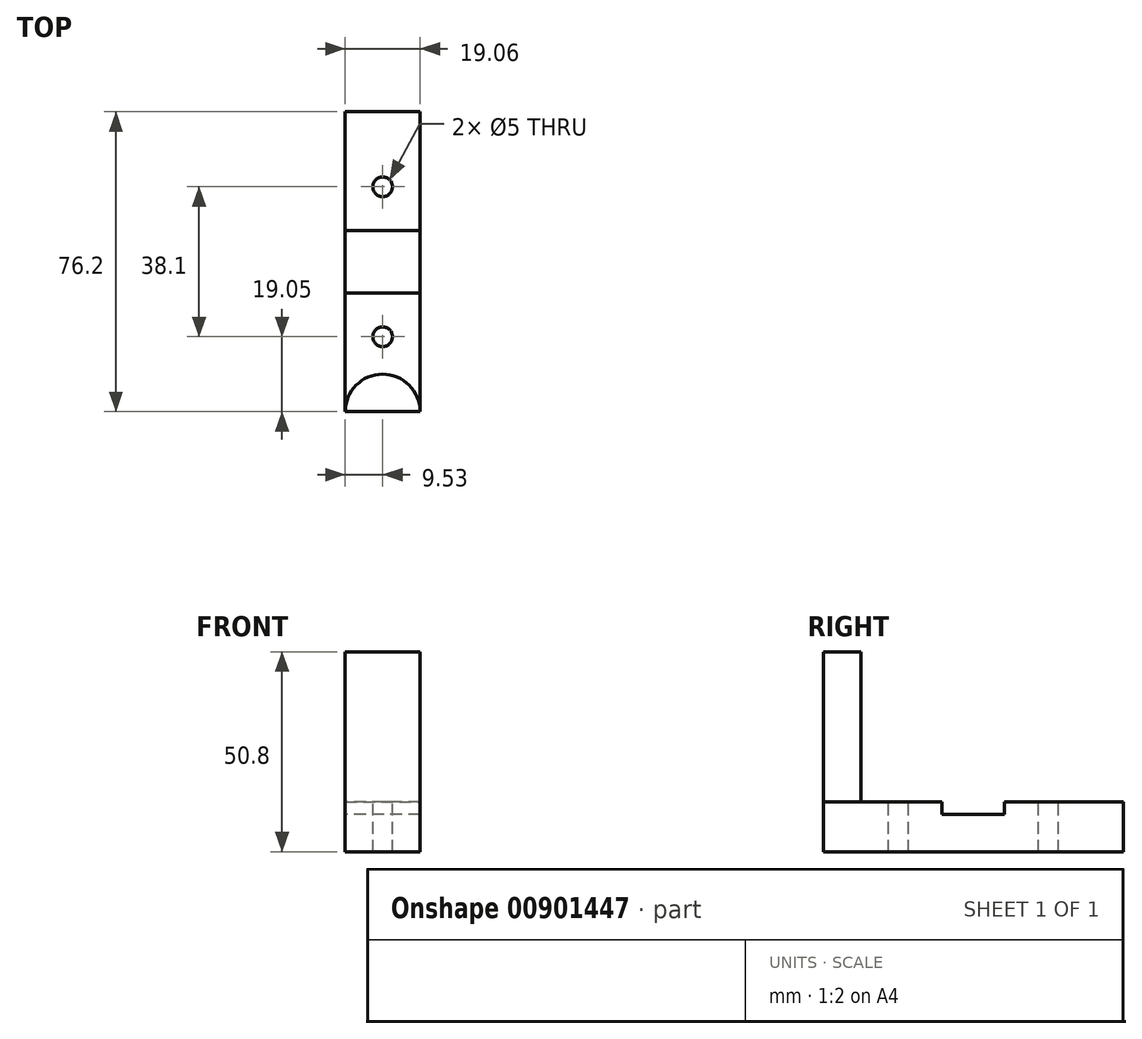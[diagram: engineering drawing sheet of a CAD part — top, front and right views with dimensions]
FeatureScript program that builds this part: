
annotation { "Feature Type Name" : "Feature", "Feature Type Description" : "" }
export const myFeature = defineFeature(function(context is Context, id is Id, definition is map)
    precondition{}
    {
        {
            var Q0;
            Q0=qCreatedBy(makeId("Top.planeOp"),FACE);
            var sketch = newSketch(context, id + "F0", { "sketchPlane" : qUnion([Q0])});
            skLineSegment(sketch, "E0.bottom", {"start": v(9.53, -38.1) * mm, "end": v(-9.52, -38.1) * mm});
            skLineSegment(sketch, "E0.top", {"start": v(9.52, 38.1) * mm, "end": v(-9.53, 38.1) * mm});
            skLineSegment(sketch, "E0.left", {"start": v(9.53, -38.1) * mm, "end": v(9.52, 38.1) * mm});
            skLineSegment(sketch, "E0.right", {"start": v(-9.52, -38.1) * mm, "end": v(-9.53, 38.1) * mm});
            skPoint(sketch, "E0.middle", {"position": v(0, 0) * mm});
            skSolve(sketch);
        }
        {
            var Q0;
            Q0 = qSketchRegion(id + "F0", true);
            extrude(context, id + "F1", {"entities" : qUnion([Q0]), "depth" : 12.7 * mm, "offsetDistance" : 25.4 * mm});
        }
        {
            var Q0;
            Q0=makeQuery(id+"F1.opExtrude","CAP_FACE",FACE,{"disambiguationData":[OSD([sQuery(id+"F0.wireOp",EDGE,"E0.bottom"),sQuery(id+"F0.wireOp",EDGE,"E0.top"),sQuery(id+"F0.wireOp",EDGE,"E0.left"),sQuery(id+"F0.wireOp",EDGE,"E0.right")])],"isStart":false});
            var sketch = newSketch(context, id + "F2", { "sketchPlane" : qUnion([Q0])});
            skArc(sketch, "E1", {"start": v(9.53, -38.1) * mm, "mid": v(0, -28.57) * mm, "end": v(-9.53, -38.1) * mm});
            skPoint(sketch, "E1.first.point", {"position": v(-9.52, -38.1) * mm});
            skPoint(sketch, "E1.second.point", {"position": v(9.53, -38.1) * mm});
            skPoint(sketch, "E1.third.point", {"position": v(0, -28.57) * mm});
            skPoint(sketch, "E1.third.point.positionSnap0", {"position": v(0, -38.1) * mm});
            skLineSegment(sketch, "E2", {"start": v(9.53, -38.1) * mm, "end": v(-9.52, -38.1) * mm});
            skSolve(sketch);
        }
        {
            var Q0;
            Q0 = qSketchRegion(id + "F2", true);
            extrude(context, id + "F3", {"entities" : qUnion([Q0]), "operationType" : NewBodyOperationType.ADD, "depth" : 38.1 * mm, "offsetDistance" : 25.4 * mm});
        }
        {
            var Q0;
            Q0=makeQuery(id+"F1.opExtrude","SWEPT_FACE",FACE,{"disambiguationData":[OSD([sQuery(id+"F0.wireOp",EDGE,"E0.right")])]});
            var sketch = newSketch(context, id + "F4", { "sketchPlane" : qUnion([Q0])});
            skLineSegment(sketch, "E3.bottom", {"start": v(7.94, 9.53) * mm, "end": v(-7.94, 9.53) * mm});
            skLineSegment(sketch, "E3.top", {"start": v(7.94, 15.88) * mm, "end": v(-7.94, 15.88) * mm});
            skLineSegment(sketch, "E3.left", {"start": v(7.94, 9.53) * mm, "end": v(7.94, 15.88) * mm});
            skLineSegment(sketch, "E3.right", {"start": v(-7.94, 9.53) * mm, "end": v(-7.94, 15.88) * mm});
            skPoint(sketch, "E3.middle", {"position": v(0, 12.7) * mm});
            skSolve(sketch);
        }
        {
            var Q0;
            Q0 = qSketchRegion(id + "F4", true);
            extrude(context, id + "F5", {"entities" : qUnion([Q0]), "operationType" : NewBodyOperationType.REMOVE, "endBound" : BoundingType.THROUGH_ALL, "oppositeDirection" : true, "depth" : 25.4 * mm, "offsetDistance" : 25.4 * mm});
        }
        {
            var Q0;
            {var subQ0=sQuery(id+"F0.wireOp",EDGE,"E0.top");var subQ1=sQuery(id+"F0.wireOp",EDGE,"E0.left");var subQ2=sQuery(id+"F0.wireOp",EDGE,"E0.right");Q0=makeQuery(id+"F5.boolean.opBoolean","SPLIT",FACE,{"disambiguationData":[TD([makeQuery(id+"F1.opExtrude","SWEPT_FACE",FACE,{"disambiguationData":[OSD([subQ0])]})])],"derivedFrom":makeQuery(id+"F1.opExtrude","CAP_FACE",FACE,{"disambiguationData":[OSD([sQuery(id+"F0.wireOp",EDGE,"E0.bottom"),subQ0,subQ1,subQ2])],"isStart":false})});}
            var sketch = newSketch(context, id + "F6", { "sketchPlane" : qUnion([Q0])});
            skCircle(sketch, "E4", {"center": v(0, -19.05) * mm, "radius": 2.5 * mm});
            skCircle(sketch, "E5.MirrorC", {"center": v(0, 19.05) * mm, "radius": 2.5 * mm});
            skSolve(sketch);
        }
        {
            var Q0;
            Q0 = qSketchRegion(id + "F6", true);
            extrude(context, id + "F7", {"entities" : qUnion([Q0]), "operationType" : NewBodyOperationType.REMOVE, "endBound" : BoundingType.THROUGH_ALL, "oppositeDirection" : true, "depth" : 25.4 * mm, "offsetDistance" : 25.4 * mm});
        }
    });
